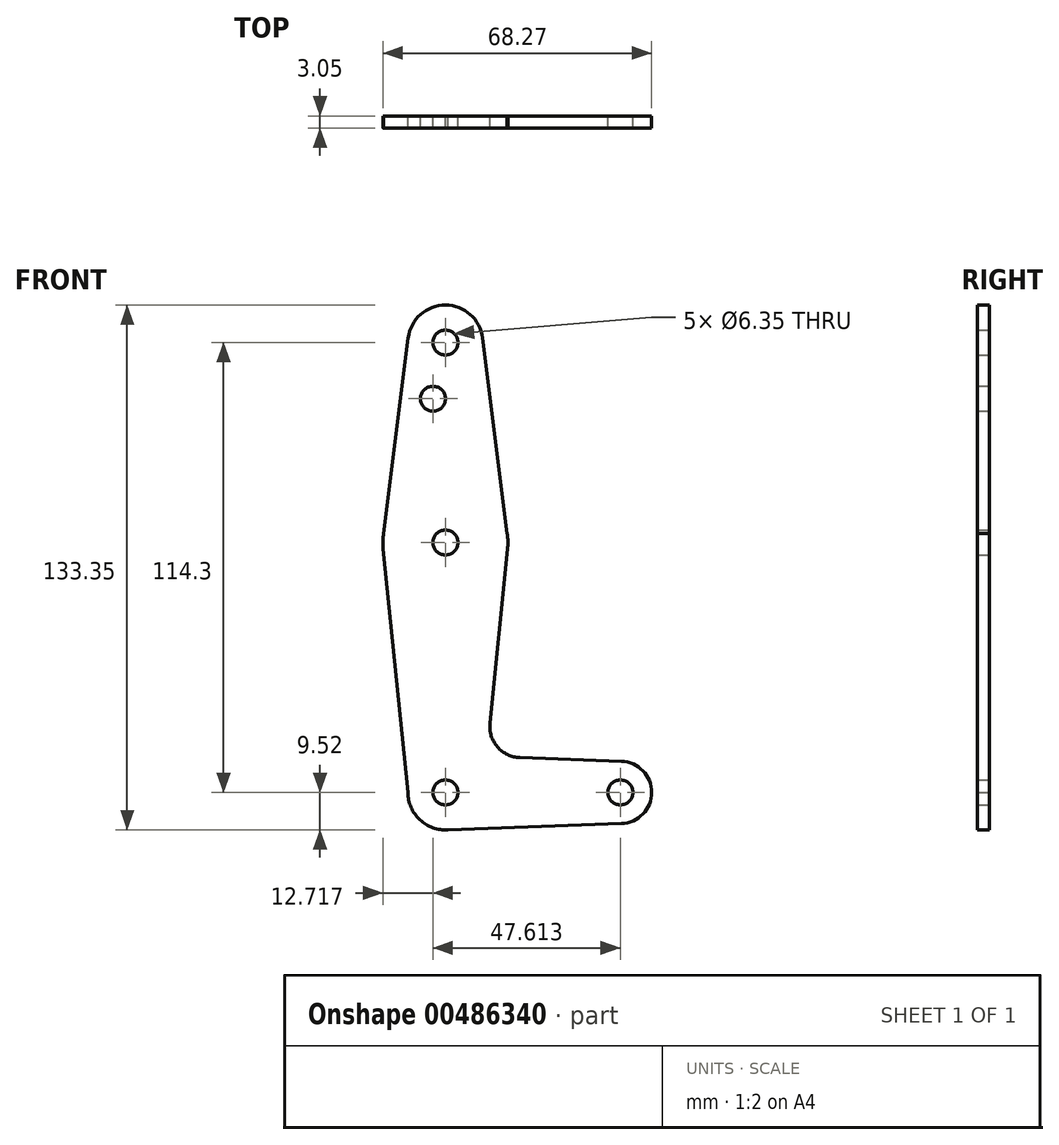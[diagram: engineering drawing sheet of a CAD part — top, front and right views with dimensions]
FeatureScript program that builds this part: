
annotation { "Feature Type Name" : "Feature", "Feature Type Description" : "" }
export const myFeature = defineFeature(function(context is Context, id is Id, definition is map)
    precondition{}
    {
        {
            var Q0;
            Q0=qCreatedBy(makeId("Front.planeOp"),FACE);
            var sketch = newSketch(context, id + "F0", { "sketchPlane" : qUnion([Q0])});
            skLineSegment(sketch, "E0", {"start": v(0, 114.3) * mm, "end": v(0, 0) * mm, "construction": true});
            skLineSegment(sketch, "E1", {"start": v(0, 0) * mm, "end": v(44.45, 0) * mm, "construction": true});
            skCircle(sketch, "E2", {"center": v(0, 114.3) * mm, "radius": 9.53 * mm});
            skCircle(sketch, "E3", {"center": v(0, 0) * mm, "radius": 9.53 * mm});
            skCircle(sketch, "E4", {"center": v(44.45, 0) * mm, "radius": 7.94 * mm});
            skLineSegment(sketch, "E5", {"start": v(0, -9.52) * mm, "end": v(44.73, -7.93) * mm});
            skLineSegment(sketch, "E6", {"start": v(44.73, 7.93) * mm, "end": v(18.93, 8.85) * mm});
            skCircle(sketch, "E7", {"center": v(0, 114.3) * mm, "radius": 3.18 * mm});
            skCircle(sketch, "E8", {"center": v(0, 0) * mm, "radius": 3.18 * mm});
            skCircle(sketch, "E9", {"center": v(44.45, 0) * mm, "radius": 3.18 * mm});
            skCircle(sketch, "E10", {"center": v(-3.16, 100.03) * mm, "radius": 3.18 * mm});
            skCircle(sketch, "E11", {"center": v(0, 63.5) * mm, "radius": 15.88 * mm});
            skLineSegment(sketch, "E12", {"start": v(-9.52, 0) * mm, "end": v(-15.8, 61.9) * mm});
            skLineSegment(sketch, "E13", {"start": v(-15.79, 65.15) * mm, "end": v(-9.45, 115.49) * mm});
            skLineSegment(sketch, "E14", {"start": v(9.45, 115.49) * mm, "end": v(15.79, 65.15) * mm});
            skLineSegment(sketch, "E15", {"start": v(15.8, 61.9) * mm, "end": v(11.3, 17.6) * mm});
            skCircle(sketch, "E16", {"center": v(0, 63.5) * mm, "radius": 3.18 * mm});
            skArc(sketch, "E17.filletArc", {"start": v(11.3, 17.6) * mm, "mid": v(13.22, 11.57) * mm, "end": v(18.93, 8.85) * mm});
            skSolve(sketch);
        }
        {
            var Q0;
            Q0 = qSketchRegion(id + "F0", true);
            extrude(context, id + "F1", {"entities" : qUnion([Q0]), "depth" : 3.05 * mm});
        }
    });
